# Revit family: Faucet-Kitchen-KOHLER-Components-K-28268
name_source: partatom
category: Plumbing Fixtures
units: mm (PartAtom-declared; Revit-internal decimal feet)

## family parameters
Cut with Voids When Loaded = No
Host = Face
Maintain Annotation Orientation = No
OmniClass Number = 23.31.11.00
OmniClass Title = Faucets
Part Type = Normal
Room Calculation Point = No
Round Connector Dimension = Use Diameter
Shared = No

## types (1)
- Not A Type - See Type Catelog
    ADA Compliant = Yes
    Assembly Code = D2010
    CW Connection = Yes
    Cold Water Inlet = Cold Water Inlet
    Date Modified = 02/25/2025
    Default Elevation = 36"
    Description = Pull-down kitchen sink faucet with two-function sprayhead
    Drain Included = No
    Finish = Default
    Flow Rate = 2 GPM
    HW Connection = Yes
    Handle Clearance = 2 13/16"
    Height = 19 7/16"
    Hot Water Inlet = Hot Water Inlet
    Length = 9 9/16"
    Manufacturer = Kohler Co.
    Master Format 2014 = 22 41 39
    Master Format 2014 Name = Residential Faucets, Supplies, and Trim
    Material = Premiun Metal Construction
    Pressure = 60.00 psi
    Product Documentation Link = https://www.us.kohler.com
    Product Name = Components
    Product Page URL = http://www.us.kohler.com
    Secondary Finish = Default
    Spout Reach = 9 9/16"
    Tertiary Finish = Default
    Type = 0
    URL = https://www.us.kohler.com
    Vent Connection = No
    Waste Connection = No
    Waste Water Outlet = Waste Water Outlet
    WaterSense Certified = No
    Width = 2 5/16"

## geometry (parser evidence)
native form markers: Sweep x6
no freeform markers — native parametric forms only
